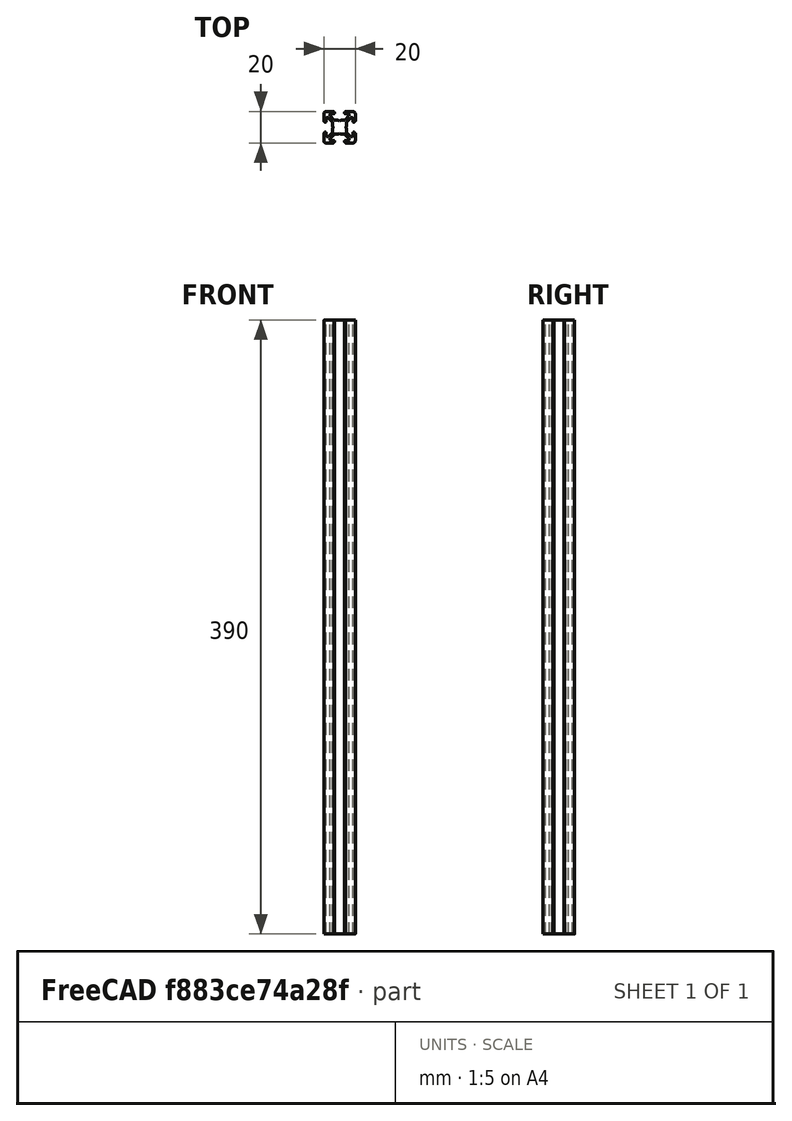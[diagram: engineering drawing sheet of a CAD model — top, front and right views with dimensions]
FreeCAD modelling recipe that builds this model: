
FCSTD DOCUMENT  (FreeCAD 0.15R4671 (Git))
Label: Perfil 390 mm
License: CC-BY 3.0
LicenseURL: http://creativecommons.org/licenses/by/3.0/
objects: Sketcher::SketchObject×2, PartDesign::Pad×1, PartDesign::Pocket×1, Part::MultiFuse×1
note: 7 computed .brp shape members not serialized (recipe doc carries the construction recipe); baked Part::Feature solids carry a one-line shape summary decoded from their .brp

FEATURE [Sketcher::SketchObject] Sketch
  Placement = pos=(1.5,0,0) rot=(0,0,1;0rad)
  sketch-geometry (136):
    g0: LineSegment StartX=0 StartY=20 StartZ=0 EndX=4.65 EndY=20 EndZ=0
    g1: ArcOfCircle CenterX=-1e-12 CenterY=18.5 CenterZ=0 NormalX=0 NormalY=0 NormalZ=1 Radius=1.5 StartAngle=1.5708 EndAngle=3.14159
    g2: LineSegment StartX=-1.5 StartY=13.85 StartZ=0 EndX=-1.5 EndY=18.5 EndZ=0
    g3: ArcOfCircle CenterX=-1.3 CenterY=13.85 CenterZ=0 NormalX=0 NormalY=0 NormalZ=1 Radius=0.2 StartAngle=3.14159 EndAngle=4.71239
    g4: LineSegment StartX=-1 StartY=13.65 StartZ=0 EndX=-1.3 EndY=13.65 EndZ=0
    g5: LineSegment StartX=-1 StartY=13.3 StartZ=0 EndX=-1 EndY=13.65 EndZ=0
    g6: ArcOfCircle CenterX=-0.8 CenterY=13.3 CenterZ=0 NormalX=0 NormalY=0 NormalZ=1 Radius=0.2 StartAngle=3.14159 EndAngle=4.71239
    g7: LineSegment StartX=-0.5 StartY=13.1 StartZ=0 EndX=-0.8 EndY=13.1 EndZ=0
    g8: ArcOfCircle CenterX=-0.5 CenterY=13.6 CenterZ=0 NormalX=0 NormalY=0 NormalZ=1 Radius=0.5 StartAngle=4.71239 EndAngle=6.28319
    g9: LineSegment StartX=2.68e-07 StartY=15.5 StartZ=0 EndX=2.68e-07 EndY=13.6 EndZ=0
    g10: ArcOfCircle CenterX=0.5 CenterY=15.5 CenterZ=0 NormalX=0 NormalY=0 NormalZ=1 Radius=0.5 StartAngle=1.5708 EndAngle=3.14159
    g11: LineSegment StartX=1.23223 StartY=16 StartZ=0 EndX=0.5 EndY=16 EndZ=0
    g12: ArcOfCircle CenterX=1.23223 CenterY=15.5 CenterZ=0 NormalX=0 NormalY=0 NormalZ=1 Radius=0.5 StartAngle=0.785398 EndAngle=1.5708
    g13: LineSegment StartX=3.85355 StartY=13.5858 StartZ=0 EndX=1.58579 EndY=15.8536 EndZ=0
    g14: ArcOfCircle CenterX=3.5 CenterY=13.2322 CenterZ=0 NormalX=0 NormalY=0 NormalZ=1 Radius=0.5 StartAngle=0 EndAngle=0.785398
    g15: LineSegment StartX=4 StartY=10.9536 StartZ=0 EndX=4 EndY=13.2322 EndZ=0
    g16: ArcOfCircle CenterX=4.2 CenterY=10.9536 CenterZ=0 NormalX=0 NormalY=0 NormalZ=1 Radius=0.2 StartAngle=3.14159 EndAngle=3.66519
    g17: LineSegment StartX=4.46188 StartY=10.1 StartZ=0 EndX=4.0268 EndY=10.8536 EndZ=0
    g18: ArcOfCircle CenterX=4.28868 CenterY=10 CenterZ=0 NormalX=0 NormalY=0 NormalZ=1 Radius=0.2 StartAngle=5.75959 EndAngle=6.80678
    g19: LineSegment StartX=4.0268 StartY=9.14641 StartZ=0 EndX=4.46188 EndY=9.9 EndZ=0
    g20: ArcOfCircle CenterX=4.2 CenterY=9.04641 CenterZ=0 NormalX=0 NormalY=0 NormalZ=1 Radius=0.2 StartAngle=2.61799 EndAngle=3.14159
    g21: LineSegment StartX=4 StartY=6.76777 StartZ=0 EndX=4 EndY=9.04641 EndZ=0
    g22: ArcOfCircle CenterX=3.5 CenterY=6.76777 CenterZ=0 NormalX=0 NormalY=0 NormalZ=1 Radius=0.5 StartAngle=5.49779 EndAngle=6.28319
    g23: LineSegment StartX=1.58579 StartY=4.14645 StartZ=0 EndX=3.85355 EndY=6.41421 EndZ=0
    g24: ArcOfCircle CenterX=1.23223 CenterY=4.5 CenterZ=0 NormalX=0 NormalY=0 NormalZ=1 Radius=0.5 StartAngle=4.71239 EndAngle=5.49779
    g25: LineSegment StartX=0.5 StartY=4 StartZ=0 EndX=1.23223 EndY=4 EndZ=0
    g26: ArcOfCircle CenterX=0.5 CenterY=4.5 CenterZ=0 NormalX=0 NormalY=0 NormalZ=1 Radius=0.5 StartAngle=3.14159 EndAngle=4.71239
    g27: LineSegment StartX=2.68e-07 StartY=6.4 StartZ=0 EndX=2.68e-07 EndY=4.5 EndZ=0
    g28: ArcOfCircle CenterX=-0.5 CenterY=6.4 CenterZ=0 NormalX=0 NormalY=0 NormalZ=1 Radius=0.5 StartAngle=0 EndAngle=1.5708
    g29: LineSegment StartX=-0.8 StartY=6.9 StartZ=0 EndX=-0.5 EndY=6.9 EndZ=0
    g30: ArcOfCircle CenterX=-0.8 CenterY=6.7 CenterZ=0 NormalX=0 NormalY=0 NormalZ=1 Radius=0.2 StartAngle=1.5708 EndAngle=3.14159
    g31: LineSegment StartX=-1 StartY=6.35 StartZ=0 EndX=-1 EndY=6.7 EndZ=0
    g32: LineSegment StartX=-1.3 StartY=6.35 StartZ=0 EndX=-1 EndY=6.35 EndZ=0
    g33: ArcOfCircle CenterX=-1.3 CenterY=6.15 CenterZ=0 NormalX=0 NormalY=0 NormalZ=1 Radius=0.2 StartAngle=1.5708 EndAngle=3.14159
    g34: LineSegment StartX=-1.5 StartY=1.5 StartZ=0 EndX=-1.5 EndY=6.15 EndZ=0
    g35: ArcOfCircle CenterX=0 CenterY=1.5 CenterZ=0 NormalX=0 NormalY=0 NormalZ=1 Radius=1.5 StartAngle=3.14159 EndAngle=4.71239
    g36: LineSegment StartX=4.65 StartY=1e-12 StartZ=0 EndX=0 EndY=0 EndZ=0
    g37: ArcOfCircle CenterX=4.65 CenterY=0.2 CenterZ=0 NormalX=0 NormalY=0 NormalZ=1 Radius=0.2 StartAngle=4.71239 EndAngle=6.28319
    g38: LineSegment StartX=4.85 StartY=0.5 StartZ=0 EndX=4.85 EndY=0.2 EndZ=0
    g39: LineSegment StartX=5.2 StartY=0.5 StartZ=0 EndX=4.85 EndY=0.5 EndZ=0
    g40: ArcOfCircle CenterX=5.2 CenterY=0.7 CenterZ=0 NormalX=0 NormalY=0 NormalZ=1 Radius=0.2 StartAngle=4.71239 EndAngle=6.28319
    g41: LineSegment StartX=5.4 StartY=1 StartZ=0 EndX=5.4 EndY=0.7 EndZ=0
    g42: ArcOfCircle CenterX=4.9 CenterY=1 CenterZ=0 NormalX=0 NormalY=0 NormalZ=1 Radius=0.5 StartAngle=0 EndAngle=1.5708
    g43: LineSegment StartX=3 StartY=1.5 StartZ=0 EndX=4.9 EndY=1.5 EndZ=0
    g44: ArcOfCircle CenterX=3 CenterY=2 CenterZ=0 NormalX=0 NormalY=0 NormalZ=1 Radius=0.5 StartAngle=3.14159 EndAngle=4.71239
    g45: LineSegment StartX=2.5 StartY=2.73223 StartZ=0 EndX=2.5 EndY=2 EndZ=0
    g46: ArcOfCircle CenterX=3 CenterY=2.73223 CenterZ=0 NormalX=0 NormalY=0 NormalZ=1 Radius=0.5 StartAngle=2.35619 EndAngle=3.14159
    g47: LineSegment StartX=4.91421 StartY=5.35355 StartZ=0 EndX=2.64645 EndY=3.08579 EndZ=0
    g48: ArcOfCircle CenterX=5.26777 CenterY=5 CenterZ=0 NormalX=0 NormalY=0 NormalZ=1 Radius=0.5 StartAngle=1.5708 EndAngle=2.35619
    g49: LineSegment StartX=7.54641 StartY=5.5 StartZ=0 EndX=5.26777 EndY=5.5 EndZ=0
    g50: ArcOfCircle CenterX=7.54641 CenterY=5.7 CenterZ=0 NormalX=0 NormalY=0 NormalZ=1 Radius=0.2 StartAngle=4.71239 EndAngle=5.23599
    g51: LineSegment StartX=8.4 StartY=5.96188 StartZ=0 EndX=7.64641 EndY=5.52679 EndZ=0
    g52: ArcOfCircle CenterX=8.5 CenterY=5.78868 CenterZ=0 NormalX=0 NormalY=0 NormalZ=1 Radius=0.2 StartAngle=1.0472 EndAngle=2.0944
    g53: LineSegment StartX=9.35359 StartY=5.52679 StartZ=0 EndX=8.6 EndY=5.96188 EndZ=0
    g54: ArcOfCircle CenterX=9.45359 CenterY=5.7 CenterZ=0 NormalX=0 NormalY=0 NormalZ=1 Radius=0.2 StartAngle=4.18879 EndAngle=4.71239
    g55: LineSegment StartX=11.7322 StartY=5.5 StartZ=0 EndX=9.45359 EndY=5.5 EndZ=0
    g56: ArcOfCircle CenterX=11.7322 CenterY=5 CenterZ=0 NormalX=0 NormalY=0 NormalZ=1 Radius=0.5 StartAngle=0.785398 EndAngle=1.5708
    g57: LineSegment StartX=14.3536 StartY=3.08579 StartZ=0 EndX=12.0858 EndY=5.35355 EndZ=0
    g58: ArcOfCircle CenterX=14 CenterY=2.73223 CenterZ=0 NormalX=0 NormalY=0 NormalZ=1 Radius=0.5 StartAngle=0 EndAngle=0.785398
    g59: LineSegment StartX=14.5 StartY=2 StartZ=0 EndX=14.5 EndY=2.73223 EndZ=0
    g60: ArcOfCircle CenterX=14 CenterY=2 CenterZ=0 NormalX=0 NormalY=0 NormalZ=1 Radius=0.5 StartAngle=4.71239 EndAngle=6.28319
    g61: LineSegment StartX=12.1 StartY=1.5 StartZ=0 EndX=14 EndY=1.5 EndZ=0
    g62: ArcOfCircle CenterX=12.1 CenterY=1 CenterZ=0 NormalX=0 NormalY=0 NormalZ=1 Radius=0.5 StartAngle=1.5708 EndAngle=3.14159
    g63: LineSegment StartX=11.6 StartY=0.7 StartZ=0 EndX=11.6 EndY=1 EndZ=0
    g64: ArcOfCircle CenterX=11.8 CenterY=0.7 CenterZ=0 NormalX=0 NormalY=0 NormalZ=1 Radius=0.2 StartAngle=3.14159 EndAngle=4.71239
    g65: LineSegment StartX=12.15 StartY=0.5 StartZ=0 EndX=11.8 EndY=0.5 EndZ=0
    g66: LineSegment StartX=12.15 StartY=0.2 StartZ=0 EndX=12.15 EndY=0.5 EndZ=0
    g67: ArcOfCircle CenterX=12.35 CenterY=0.2 CenterZ=0 NormalX=0 NormalY=0 NormalZ=1 Radius=0.2 StartAngle=3.14159 EndAngle=4.71239
    g68: LineSegment StartX=17 StartY=1e-12 StartZ=0 EndX=12.35 EndY=0 EndZ=0
    g69: ArcOfCircle CenterX=17 CenterY=1.5 CenterZ=0 NormalX=0 NormalY=0 NormalZ=1 Radius=1.5 StartAngle=4.71239 EndAngle=6.28319
    g70: LineSegment StartX=18.5 StartY=6.15 StartZ=0 EndX=18.5 EndY=1.5 EndZ=0
    g71: ArcOfCircle CenterX=18.3 CenterY=6.15 CenterZ=0 NormalX=0 NormalY=0 NormalZ=1 Radius=0.2 StartAngle=0 EndAngle=1.5708
    g72: LineSegment StartX=18 StartY=6.35 StartZ=0 EndX=18.3 EndY=6.35 EndZ=0
    g73: LineSegment StartX=18 StartY=6.7 StartZ=0 EndX=18 EndY=6.35 EndZ=0
    g74: ArcOfCircle CenterX=17.8 CenterY=6.7 CenterZ=0 NormalX=0 NormalY=0 NormalZ=1 Radius=0.2 StartAngle=0 EndAngle=1.5708
    g75: LineSegment StartX=17.5 StartY=6.9 StartZ=0 EndX=17.8 EndY=6.9 EndZ=0
    g76: ArcOfCircle CenterX=17.5 CenterY=6.4 CenterZ=0 NormalX=0 NormalY=0 NormalZ=1 Radius=0.5 StartAngle=1.5708 EndAngle=3.14159
    g77: LineSegment StartX=17 StartY=4.5 StartZ=0 EndX=17 EndY=6.4 EndZ=0
    g78: ArcOfCircle CenterX=16.5 CenterY=4.5 CenterZ=0 NormalX=0 NormalY=0 NormalZ=1 Radius=0.5 StartAngle=4.71239 EndAngle=6.28319
    g79: LineSegment StartX=15.7678 StartY=4 StartZ=0 EndX=16.5 EndY=4 EndZ=0
    g80: ArcOfCircle CenterX=15.7678 CenterY=4.5 CenterZ=0 NormalX=0 NormalY=0 NormalZ=1 Radius=0.5 StartAngle=3.92699 EndAngle=4.71239
    g81: LineSegment StartX=13.1464 StartY=6.41421 StartZ=0 EndX=15.4142 EndY=4.14645 EndZ=0
    g82: ArcOfCircle CenterX=13.5 CenterY=6.76777 CenterZ=0 NormalX=0 NormalY=0 NormalZ=1 Radius=0.5 StartAngle=3.14159 EndAngle=3.92699
    g83: LineSegment StartX=13 StartY=9.04641 StartZ=0 EndX=13 EndY=6.76777 EndZ=0
    g84: ArcOfCircle CenterX=12.8 CenterY=9.04641 CenterZ=0 NormalX=0 NormalY=0 NormalZ=1 Radius=0.2 StartAngle=0 EndAngle=0.523599
    g85: LineSegment StartX=12.5381 StartY=9.9 StartZ=0 EndX=12.9732 EndY=9.14641 EndZ=0
    g86: ArcOfCircle CenterX=12.7113 CenterY=10 CenterZ=0 NormalX=0 NormalY=0 NormalZ=1 Radius=0.2 StartAngle=2.61799 EndAngle=3.66519
    g87: LineSegment StartX=12.9732 StartY=10.8536 StartZ=0 EndX=12.5381 EndY=10.1 EndZ=0
    g88: ArcOfCircle CenterX=12.8 CenterY=10.9536 CenterZ=0 NormalX=0 NormalY=0 NormalZ=1 Radius=0.2 StartAngle=5.75959 EndAngle=6.28319
    g89: LineSegment StartX=13 StartY=13.2322 StartZ=0 EndX=13 EndY=10.9536 EndZ=0
    g90: ArcOfCircle CenterX=13.5 CenterY=13.2322 CenterZ=0 NormalX=0 NormalY=0 NormalZ=1 Radius=0.5 StartAngle=2.35619 EndAngle=3.14159
    g91: LineSegment StartX=15.4142 StartY=15.8536 StartZ=0 EndX=13.1464 EndY=13.5858 EndZ=0
    g92: ArcOfCircle CenterX=15.7678 CenterY=15.5 CenterZ=0 NormalX=0 NormalY=0 NormalZ=1 Radius=0.5 StartAngle=1.5708 EndAngle=2.35619
    g93: LineSegment StartX=16.5 StartY=16 StartZ=0 EndX=15.7678 EndY=16 EndZ=0
    g94: ArcOfCircle CenterX=16.5 CenterY=15.5 CenterZ=0 NormalX=0 NormalY=0 NormalZ=1 Radius=0.5 StartAngle=0 EndAngle=1.5708
    g95: LineSegment StartX=17 StartY=13.6 StartZ=0 EndX=17 EndY=15.5 EndZ=0
    g96: ArcOfCircle CenterX=17.5 CenterY=13.6 CenterZ=0 NormalX=0 NormalY=0 NormalZ=1 Radius=0.5 StartAngle=3.14159 EndAngle=4.71239
    g97: LineSegment StartX=17.8 StartY=13.1 StartZ=0 EndX=17.5 EndY=13.1 EndZ=0
    g98: ArcOfCircle CenterX=17.8 CenterY=13.3 CenterZ=0 NormalX=0 NormalY=0 NormalZ=1 Radius=0.2 StartAngle=4.71239 EndAngle=6.28319
    g99: LineSegment StartX=18 StartY=13.65 StartZ=0 EndX=18 EndY=13.3 EndZ=0
    g100: LineSegment StartX=18.3 StartY=13.65 StartZ=0 EndX=18 EndY=13.65 EndZ=0
    g101: ArcOfCircle CenterX=18.3 CenterY=13.85 CenterZ=0 NormalX=0 NormalY=0 NormalZ=1 Radius=0.2 StartAngle=4.71239 EndAngle=6.28319
    g102: LineSegment StartX=18.5 StartY=18.5 StartZ=0 EndX=18.5 EndY=13.85 EndZ=0
    g103: ArcOfCircle CenterX=17 CenterY=18.5 CenterZ=0 NormalX=0 NormalY=0 NormalZ=1 Radius=1.5 StartAngle=0 EndAngle=1.5708
    g104: LineSegment StartX=12.35 StartY=20 StartZ=0 EndX=17 EndY=20 EndZ=0
    g105: ArcOfCircle CenterX=12.35 CenterY=19.8 CenterZ=0 NormalX=0 NormalY=0 NormalZ=1 Radius=0.2 StartAngle=1.5708 EndAngle=3.14159
    g106: LineSegment StartX=12.15 StartY=19.5 StartZ=0 EndX=12.15 EndY=19.8 EndZ=0
    g107: LineSegment StartX=11.8 StartY=19.5 StartZ=0 EndX=12.15 EndY=19.5 EndZ=0
    g108: ArcOfCircle CenterX=11.8 CenterY=19.3 CenterZ=0 NormalX=0 NormalY=0 NormalZ=1 Radius=0.2 StartAngle=1.5708 EndAngle=3.14159
    g109: LineSegment StartX=11.6 StartY=19 StartZ=0 EndX=11.6 EndY=19.3 EndZ=0
    g110: ArcOfCircle CenterX=12.1 CenterY=19 CenterZ=0 NormalX=0 NormalY=0 NormalZ=1 Radius=0.5 StartAngle=3.14159 EndAngle=4.71239
    g111: LineSegment StartX=14 StartY=18.5 StartZ=0 EndX=12.1 EndY=18.5 EndZ=0
    g112: ArcOfCircle CenterX=14 CenterY=18 CenterZ=0 NormalX=0 NormalY=0 NormalZ=1 Radius=0.5 StartAngle=0 EndAngle=1.5708
    g113: LineSegment StartX=14.5 StartY=17.2678 StartZ=0 EndX=14.5 EndY=18 EndZ=0
    g114: ArcOfCircle CenterX=14 CenterY=17.2678 CenterZ=0 NormalX=0 NormalY=0 NormalZ=1 Radius=0.5 StartAngle=5.49779 EndAngle=6.28319
    g115: LineSegment StartX=12.0858 StartY=14.6464 StartZ=0 EndX=14.3536 EndY=16.9142 EndZ=0
    g116: ArcOfCircle CenterX=11.7322 CenterY=15 CenterZ=0 NormalX=0 NormalY=0 NormalZ=1 Radius=0.5 StartAngle=4.71239 EndAngle=5.49779
    g117: LineSegment StartX=9.45359 StartY=14.5 StartZ=0 EndX=11.7322 EndY=14.5 EndZ=0
    g118: ArcOfCircle CenterX=9.45359 CenterY=14.3 CenterZ=0 NormalX=0 NormalY=0 NormalZ=1 Radius=0.2 StartAngle=1.5708 EndAngle=2.0944
    g119: LineSegment StartX=8.6 StartY=14.0381 StartZ=0 EndX=9.35359 EndY=14.4732 EndZ=0
    g120: ArcOfCircle CenterX=8.5 CenterY=14.2113 CenterZ=0 NormalX=0 NormalY=0 NormalZ=1 Radius=0.2 StartAngle=4.18879 EndAngle=5.23599
    g121: LineSegment StartX=7.64641 StartY=14.4732 StartZ=0 EndX=8.4 EndY=14.0381 EndZ=0
    g122: ArcOfCircle CenterX=7.54641 CenterY=14.3 CenterZ=0 NormalX=0 NormalY=0 NormalZ=1 Radius=0.2 StartAngle=1.0472 EndAngle=1.5708
    g123: LineSegment StartX=5.26777 StartY=14.5 StartZ=0 EndX=7.54641 EndY=14.5 EndZ=0
    g124: ArcOfCircle CenterX=5.26777 CenterY=15 CenterZ=0 NormalX=0 NormalY=0 NormalZ=1 Radius=0.5 StartAngle=3.92699 EndAngle=4.71239
    g125: LineSegment StartX=2.64645 StartY=16.9142 StartZ=0 EndX=4.91421 EndY=14.6464 EndZ=0
    g126: ArcOfCircle CenterX=3 CenterY=17.2678 CenterZ=0 NormalX=0 NormalY=0 NormalZ=1 Radius=0.5 StartAngle=3.14159 EndAngle=3.92699
    g127: LineSegment StartX=2.5 StartY=18 StartZ=0 EndX=2.5 EndY=17.2678 EndZ=0
    g128: ArcOfCircle CenterX=3 CenterY=18 CenterZ=0 NormalX=0 NormalY=0 NormalZ=1 Radius=0.5 StartAngle=1.5708 EndAngle=3.14159
    g129: LineSegment StartX=4.9 StartY=18.5 StartZ=0 EndX=3 EndY=18.5 EndZ=0
    g130: ArcOfCircle CenterX=4.9 CenterY=19 CenterZ=0 NormalX=0 NormalY=0 NormalZ=1 Radius=0.5 StartAngle=4.71239 EndAngle=6.28319
    g131: LineSegment StartX=5.4 StartY=19.3 StartZ=0 EndX=5.4 EndY=19 EndZ=0
    g132: ArcOfCircle CenterX=5.2 CenterY=19.3 CenterZ=0 NormalX=0 NormalY=0 NormalZ=1 Radius=0.2 StartAngle=0 EndAngle=1.5708
    g133: LineSegment StartX=4.85 StartY=19.5 StartZ=0 EndX=5.2 EndY=19.5 EndZ=0
    g134: LineSegment StartX=4.85 StartY=19.8 StartZ=0 EndX=4.85 EndY=19.5 EndZ=0
    g135: ArcOfCircle CenterX=4.65 CenterY=19.8 CenterZ=0 NormalX=0 NormalY=0 NormalZ=1 Radius=0.2 StartAngle=0 EndAngle=1.5708
  constraints (136):
    c: Coincident(g0,g1)
    c: Coincident(g135,g0)
    c: Coincident(g1,g2)
    c: Coincident(g2,g3)
    c: Coincident(g3,g4)
    c: Coincident(g4,g5)
    c: Coincident(g6,g5)
    c: Coincident(g7,g6)
    c: Coincident(g8,g7)
    c: Coincident(g9,g8)
    c: Coincident(g10,g9)
    c: Coincident(g10,g11)
    c: Coincident(g11,g12)
    c: Coincident(g12,g13)
    c: Coincident(g14,g13)
    c: Coincident(g15,g14)
    c: Coincident(g15,g16)
    c: Coincident(g16,g17)
    c: Coincident(g17,g18)
    c: Coincident(g18,g19)
    c: Coincident(g19,g20)
    c: Coincident(g20,g21)
    c: Coincident(g21,g22)
    c: Coincident(g22,g23)
    c: Coincident(g23,g24)
    c: Coincident(g24,g25)
    c: Coincident(g26,g25)
    c: Coincident(g26,g27)
    c: Coincident(g28,g27)
    c: Coincident(g28,g29)
    c: Coincident(g30,g29)
    c: Coincident(g31,g30)
    c: Coincident(g31,g32)
    c: Coincident(g32,g33)
    c: Coincident(g33,g34)
    c: Coincident(g35,g34)
    c: Coincident(g36,g35)
    c: Coincident(g37,g36)
    c: Coincident(g37,g38)
    c: Coincident(g38,g39)
    c: Coincident(g40,g39)
    c: Coincident(g40,g41)
    c: Coincident(g41,g42)
    c: Coincident(g43,g42)
    c: Coincident(g44,g43)
    c: Coincident(g44,g45)
    c: Coincident(g45,g46)
    c: Coincident(g46,g47)
    c: Coincident(g47,g48)
    c: Coincident(g49,g48)
    c: Coincident(g49,g50)
    c: Coincident(g50,g51)
    c: Coincident(g51,g52)
    c: Coincident(g53,g52)
    c: Coincident(g54,g53)
    c: Coincident(g55,g54)
    c: Coincident(g56,g55)
    c: Coincident(g56,g57)
    c: Coincident(g58,g57)
    c: Coincident(g59,g58)
    c: Coincident(g60,g59)
    c: Coincident(g61,g60)
    c: Coincident(g62,g61)
    c: Coincident(g62,g63)
    c: Coincident(g64,g63)
    c: Coincident(g65,g64)
    c: Coincident(g66,g65)
    c: Coincident(g67,g66)
    c: Coincident(g67,g68)
    c: Coincident(g69,g68)
    c: Coincident(g70,g69)
    c: Coincident(g71,g70)
    c: Coincident(g72,g71)
    c: Coincident(g73,g72)
    c: Coincident(g73,g74)
    c: Coincident(g75,g74)
    c: Coincident(g76,g75)
    c: Coincident(g76,g77)
    c: Coincident(g77,g78)
    c: Coincident(g78,g79)
    c: Coincident(g80,g79)
    c: Coincident(g81,g80)
    c: Coincident(g81,g82)
    c: Coincident(g82,g83)
    c: Coincident(g83,g84)
    c: Coincident(g85,g84)
    c: Coincident(g86,g85)
    c: Coincident(g86,g87)
    c: Coincident(g88,g87)
    c: Coincident(g88,g89)
    c: Coincident(g89,g90)
    c: Coincident(g91,g90)
    c: Coincident(g92,g91)
    c: Coincident(g93,g92)
    c: Coincident(g94,g93)
    c: Coincident(g94,g95)
    c: Coincident(g95,g96)
    c: Coincident(g96,g97)
    c: Coincident(g98,g97)
    c: Coincident(g98,g99)
    c: Coincident(g100,g99)
    c: Coincident(g100,g101)
    c: Coincident(g101,g102)
    c: Coincident(g102,g103)
    c: Coincident(g103,g104)
    c: Coincident(g104,g105)
    c: Coincident(g106,g105)
    c: Coincident(g107,g106)
    c: Coincident(g108,g107)
    c: Coincident(g109,g108)
    c: Coincident(g110,g109)
    c: Coincident(g111,g110)
    c: Coincident(g112,g111)
    c: Coincident(g112,g113)
    c: Coincident(g113,g114)
    c: Coincident(g114,g115)
    c: Coincident(g115,g116)
    c: Coincident(g117,g116)
    c: Coincident(g118,g117)
    c: Coincident(g119,g118)
    c: Coincident(g119,g120)
    c: Coincident(g121,g120)
    c: Coincident(g121,g122)
    c: Coincident(g122,g123)
    c: Coincident(g124,g123)
    c: Coincident(g124,g125)
    c: Coincident(g126,g125)
    c: Coincident(g127,g126)
    c: Coincident(g128,g127)
    c: Coincident(g129,g128)
    c: Coincident(g130,g129)
    c: Coincident(g130,g131)
    c: Coincident(g131,g132)
    c: Coincident(g133,g132)
    c: Coincident(g134,g133)
    c: Coincident(g135,g134)
FEATURE [PartDesign::Pad] Pad
  Length = 390
  Length2 = 100
  Placement = pos=(1.5,0,0) rot=(0,0,1;0rad)
  Sketch = -> Sketch
  Type = 0
FEATURE [Sketcher::SketchObject] Sketch001
  Placement = pos=(1.5,0,390) rot=(0,0,1;0rad)
  Support = -> Pad [Face138]
  sketch-geometry (16):
    g0: ArcOfCircle CenterX=8.5 CenterY=10 CenterZ=0 NormalX=0 NormalY=0 NormalZ=1 Radius=3.54978 StartAngle=2.14023 EndAngle=2.57348
    g1: LineSegment StartX=6.5861 StartY=12.9896 StartZ=0 EndX=7.24181 EndY=12.4453 EndZ=0
    g2: ArcOfCircle CenterX=8.5 CenterY=10 CenterZ=0 NormalX=0 NormalY=0 NormalZ=1 Radius=2.75 StartAngle=1.09559 EndAngle=2.046
    g3: LineSegment StartX=9.75819 StartY=12.4453 StartZ=0 EndX=10.4139 EndY=12.9896 EndZ=0
    g4: ArcOfCircle CenterX=8.5 CenterY=10 CenterZ=0 NormalX=0 NormalY=0 NormalZ=1 Radius=3.54978 StartAngle=0.568112 EndAngle=1.00136
    g5: LineSegment StartX=11.4922 StartY=11.9099 StartZ=0 EndX=10.9453 EndY=11.2582 EndZ=0
    g6: ArcOfCircle CenterX=8.5 CenterY=10 CenterZ=0 NormalX=0 NormalY=0 NormalZ=1 Radius=2.75 StartAngle=5.80798 EndAngle=6.75839
    g7: LineSegment StartX=10.9453 StartY=8.74181 StartZ=0 EndX=11.4922 EndY=8.09007 EndZ=0
    g8: ArcOfCircle CenterX=8.5 CenterY=10 CenterZ=0 NormalX=0 NormalY=0 NormalZ=1 Radius=3.54978 StartAngle=5.28183 EndAngle=5.71507
    g9: LineSegment StartX=10.4139 StartY=7.01036 StartZ=0 EndX=9.75819 EndY=7.5547 EndZ=0
    g10: ArcOfCircle CenterX=8.5 CenterY=10 CenterZ=0 NormalX=0 NormalY=0 NormalZ=1 Radius=2.75 StartAngle=4.23718 EndAngle=5.1876
    g11: LineSegment StartX=7.24181 StartY=7.5547 StartZ=0 EndX=6.5861 EndY=7.01036 EndZ=0
    g12: ArcOfCircle CenterX=8.5 CenterY=10 CenterZ=0 NormalX=0 NormalY=0 NormalZ=1 Radius=3.54978 StartAngle=3.7097 EndAngle=4.14295
    g13: LineSegment StartX=5.50783 StartY=8.09007 StartZ=0 EndX=6.0547 EndY=8.74181 EndZ=0
    g14: ArcOfCircle CenterX=8.5 CenterY=10 CenterZ=0 NormalX=0 NormalY=0 NormalZ=1 Radius=2.75 StartAngle=2.66639 EndAngle=3.6168
    g15: LineSegment StartX=6.0547 StartY=11.2582 StartZ=0 EndX=5.50783 EndY=11.9099 EndZ=0
  constraints (16):
    c: Coincident(g0,g1)
    c: Coincident(g15,g0)
    c: Coincident(g1,g2)
    c: Coincident(g3,g2)
    c: Coincident(g4,g3)
    c: Coincident(g4,g5)
    c: Coincident(g6,g5)
    c: Coincident(g7,g6)
    c: Coincident(g8,g7)
    c: Coincident(g9,g8)
    c: Coincident(g10,g9)
    c: Coincident(g11,g10)
    c: Coincident(g12,g11)
    c: Coincident(g13,g12)
    c: Coincident(g14,g13)
    c: Coincident(g15,g14)
FEATURE [PartDesign::Pocket] Pocket
  Length = 5
  Placement = pos=(1.5,0,0) rot=(0,0,1;0rad)
  Sketch = -> Sketch001
  Type = 1
FEATURE [Part::MultiFuse] Fusion  label="Perfil vertical 767,5"
  Shapes = -> [Pad,Pocket]
